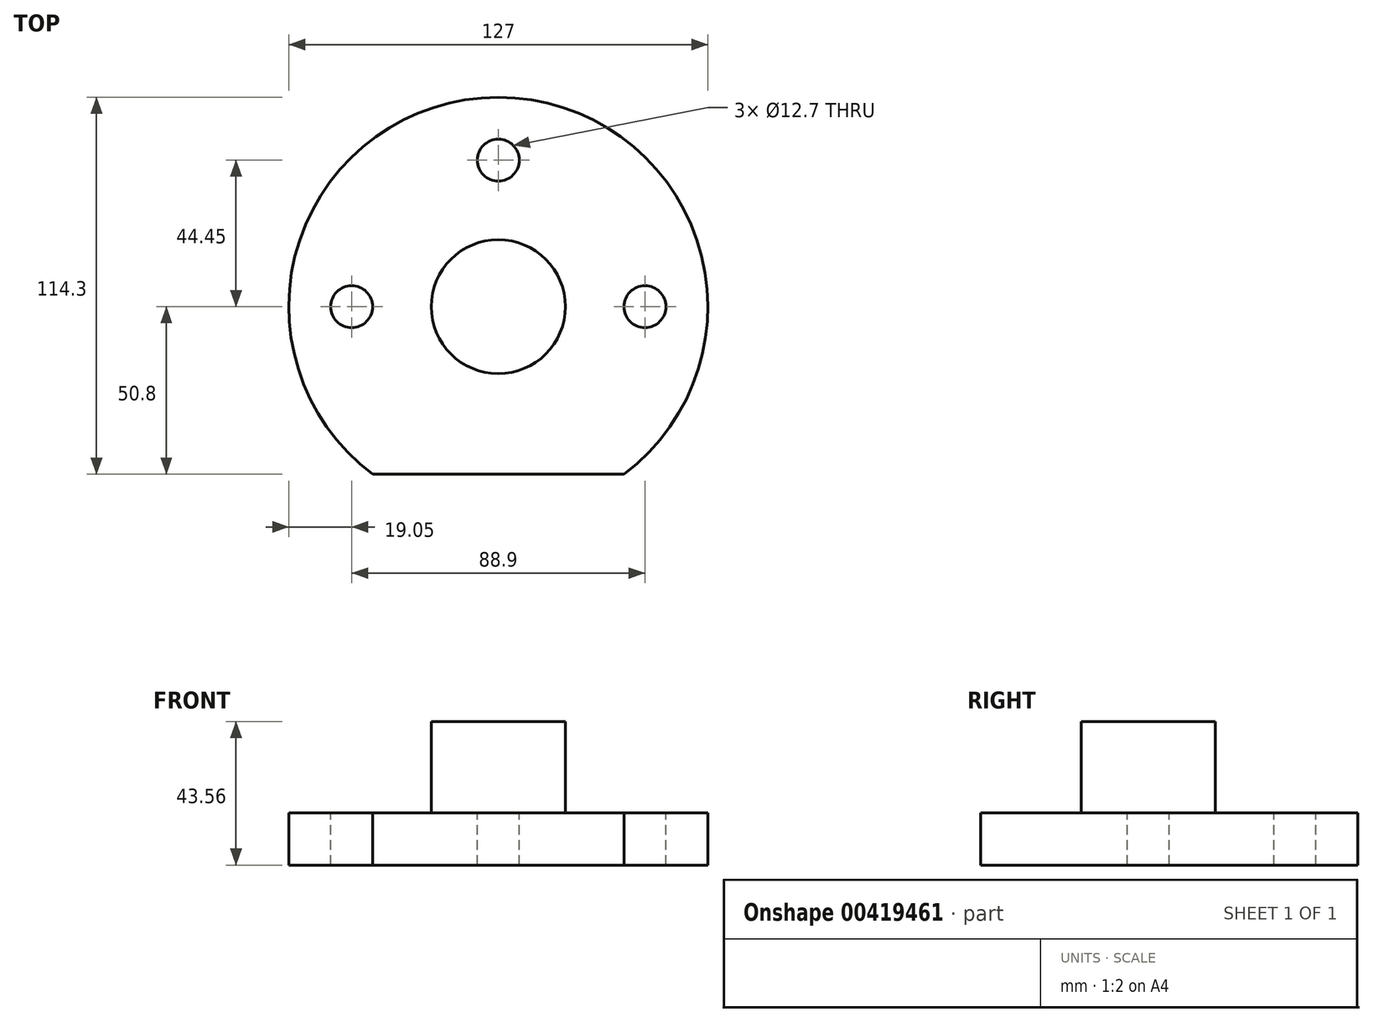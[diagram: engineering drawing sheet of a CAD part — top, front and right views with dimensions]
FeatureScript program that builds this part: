
annotation { "Feature Type Name" : "Feature", "Feature Type Description" : "" }
export const myFeature = defineFeature(function(context is Context, id is Id, definition is map)
    precondition{}
    {
        {
            var Q0;
            Q0=qCreatedBy(makeId("Top.planeOp"),FACE);
            var sketch = newSketch(context, id + "F0", { "sketchPlane" : qUnion([Q0])});
            skCircle(sketch, "E0", {"center": v(0, 0) * mm, "radius": 63.5 * mm});
            skSolve(sketch);
        }
        {
            var Q0;
            Q0 = qSketchRegion(id + "F0", true);
            extrude(context, id + "F1", {"entities" : qUnion([Q0]), "depth" : 15.88 * mm});
        }
        {
            var Q0;
            Q0=makeQuery(id+"F1.opExtrude","CAP_FACE",FACE,{"disambiguationData":[OSD([sQuery(id+"F0.wireOp",EDGE,"E0")])],"isStart":false});
            var sketch = newSketch(context, id + "F2", { "sketchPlane" : qUnion([Q0])});
            skLineSegment(sketch, "E1", {"start": v(-38.1, -50.8) * mm, "end": v(38.1, -50.8) * mm});
            skArc(sketch, "E2", {"start": v(-38.1, -50.8) * mm, "mid": v(0, -63.5) * mm, "end": v(38.1, -50.8) * mm});
            skSolve(sketch);
        }
        {
            var Q0;
            Q0 = qSketchRegion(id + "F2", true);
            extrude(context, id + "F3", {"entities" : qUnion([Q0]), "operationType" : NewBodyOperationType.REMOVE, "oppositeDirection" : true, "depth" : 25.4 * mm});
        }
        {
            var Q0;
            Q0=makeQuery(id+"F1.opExtrude","SWEPT_BODY",BODY,{"disambiguationData":[OSD([sQuery(id+"F0.wireOp",EDGE,"E0")])]});
            transform(context, id + "F4", {"entities" : qUnion([Q0]), "transformType" : TransformType.TRANSLATION_3D, "dx" : 0 * mm, "dy" : 0 * mm, "dz" : 0 * mm, "makeCopy" : true});
        }
        {
            var Q0;
            Q0=makeQuery(id+"F1.opExtrude","SWEPT_BODY",BODY,{"disambiguationData":[OSD([sQuery(id+"F0.wireOp",EDGE,"E0")])]});
            transform(context, id + "F5", {"entities" : qUnion([Q0]), "transformType" : TransformType.TRANSLATION_3D, "dx" : 0 * mm, "dy" : 0 * mm, "dz" : 0 * mm, "makeCopy" : true});
        }
        {
            var Q0;
            Q0=makeQuery(id+"F1.opExtrude","CAP_FACE",FACE,{"disambiguationData":[OSD([sQuery(id+"F0.wireOp",EDGE,"E0")])],"isStart":false});
            var sketch = newSketch(context, id + "F6", { "sketchPlane" : qUnion([Q0])});
            skCircle(sketch, "E3", {"center": v(0, 0) * mm, "radius": 44.45 * mm, "construction": true});
            skCircle(sketch, "E4", {"center": v(0, 44.45) * mm, "radius": 6.35 * mm});
            skCircle(sketch, "E5", {"center": v(44.45, 0) * mm, "radius": 6.35 * mm});
            skCircle(sketch, "E6", {"center": v(-44.45, 0) * mm, "radius": 6.35 * mm});
            skSolve(sketch);
        }
        {
            var Q0;
            Q0=makeQuery(id+"F6.imprint","IMPRINT",FACE,{"disambiguationData":[TD([[makeQuery(id+"F6.imprint","IMPRINT",EDGE,{"derivedFrom":sQuery(id+"F6.wireOp",EDGE,"E5")}),1.0]])]});
            var Q1;
            Q1=makeQuery(id+"F6.imprint","IMPRINT",FACE,{"disambiguationData":[TD([[makeQuery(id+"F6.imprint","IMPRINT",EDGE,{"derivedFrom":sQuery(id+"F6.wireOp",EDGE,"E4")}),1.0]])]});
            var Q2;
            Q2=makeQuery(id+"F6.imprint","IMPRINT",FACE,{"disambiguationData":[TD([[makeQuery(id+"F6.imprint","IMPRINT",EDGE,{"derivedFrom":sQuery(id+"F6.wireOp",EDGE,"E6")}),1.0]])]});
            extrude(context, id + "F7", {"entities" : qUnion([Q0, Q1, Q2]), "operationType" : NewBodyOperationType.REMOVE, "oppositeDirection" : true, "depth" : 25.4 * mm});
        }
        {
            var Q0;
            Q0=makeQuery(id+"F4.opPattern","COPY",FACE,{"derivedFrom":makeQuery(id+"F1.opExtrude","CAP_FACE",FACE,{"disambiguationData":[OSD([sQuery(id+"F0.wireOp",EDGE,"E0")])],"isStart":false}),"instanceName":"1"});
            var sketch = newSketch(context, id + "F8", { "sketchPlane" : qUnion([Q0])});
            skCircle(sketch, "E7", {"center": v(0, 3.13) * mm, "radius": 20.32 * mm});
            skSolve(sketch);
        }
        {
            var Q0;
            Q0 = qSketchRegion(id + "F8", true);
            extrude(context, id + "F9", {"entities" : qUnion([Q0]), "depth" : 27.94 * mm});
        }
        {
            var Q0;
            Q0=makeQuery(id+"F9.opExtrude","SWEPT_BODY",BODY,{"disambiguationData":[OSD([sQuery(id+"F8.wireOp",EDGE,"E7")])]});
            var Q1;
            Q1=makeQuery(id+"F5.opPattern","COPY",BODY,{"derivedFrom":makeQuery(id+"F1.opExtrude","SWEPT_BODY",BODY,{"disambiguationData":[OSD([sQuery(id+"F0.wireOp",EDGE,"E0")])]}),"instanceName":"1"});
            var Q2;
            Q2=makeQuery(id+"F4.opPattern","COPY",BODY,{"derivedFrom":makeQuery(id+"F1.opExtrude","SWEPT_BODY",BODY,{"disambiguationData":[OSD([sQuery(id+"F0.wireOp",EDGE,"E0")])]}),"instanceName":"1"});
            deleteBodies(context, id + "F10", {"entities" : qUnion([Q0, Q1, Q2])});
        }
        {
            var Q0;
            Q0=makeQuery(id+"F1.opExtrude","CAP_FACE",FACE,{"disambiguationData":[OSD([sQuery(id+"F0.wireOp",EDGE,"E0")])],"isStart":false});
            var sketch = newSketch(context, id + "F11", { "sketchPlane" : qUnion([Q0])});
            skCircle(sketch, "E8", {"center": v(0, 0) * mm, "radius": 20.32 * mm});
            skSolve(sketch);
        }
        {
            var Q0;
            Q0 = qSketchRegion(id + "F11", true);
            extrude(context, id + "F12", {"entities" : qUnion([Q0]), "operationType" : NewBodyOperationType.ADD, "depth" : 27.7 * mm});
        }
    });
